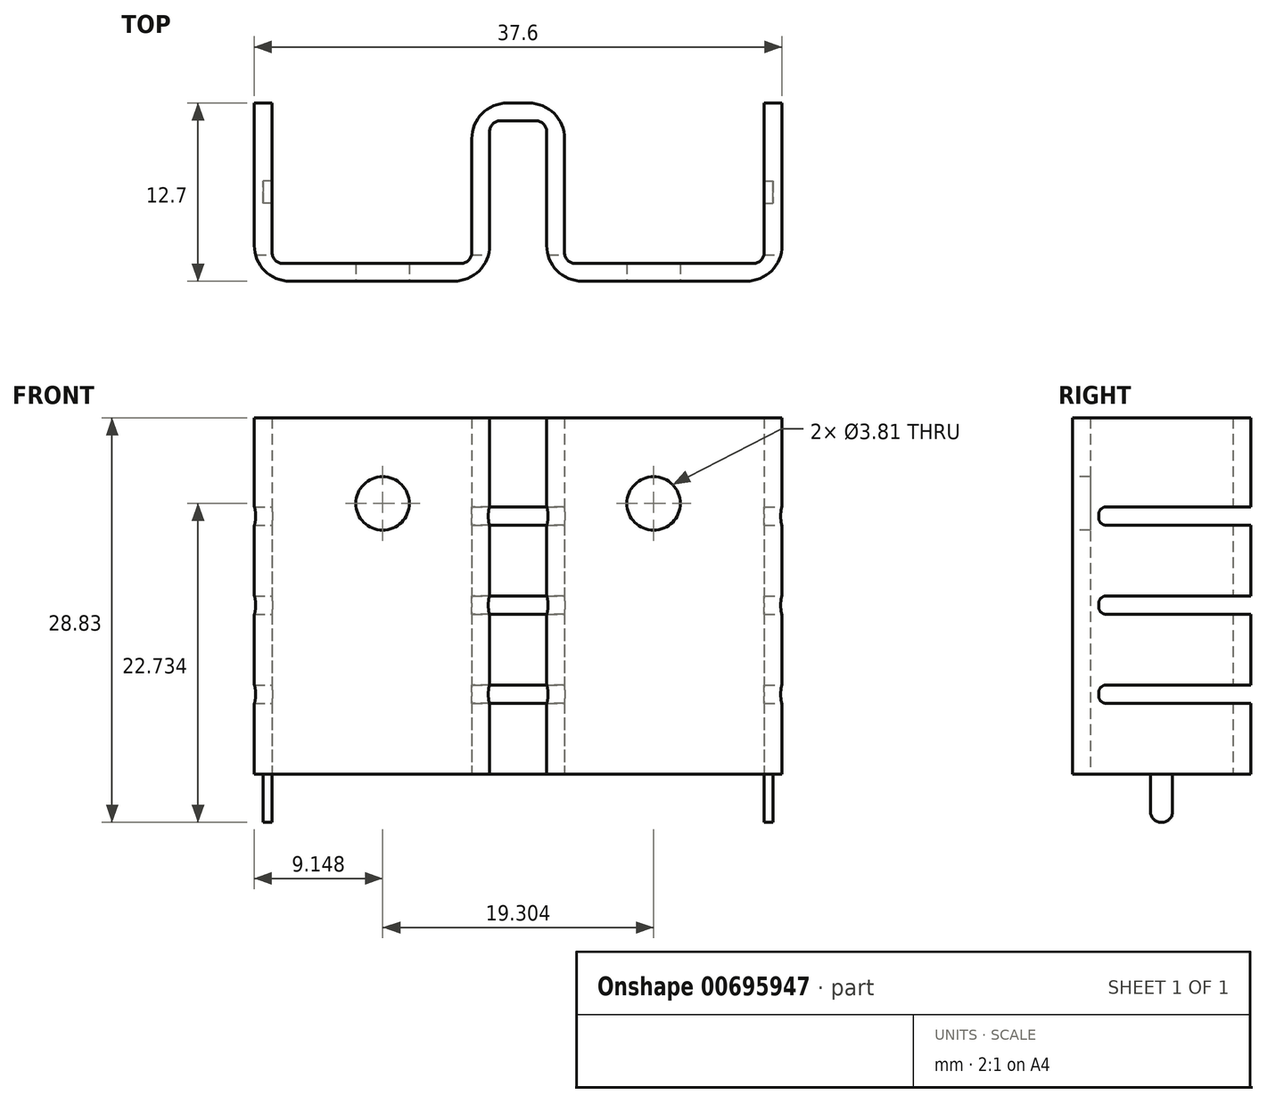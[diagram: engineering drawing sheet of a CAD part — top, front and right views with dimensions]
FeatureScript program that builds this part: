
annotation { "Feature Type Name" : "Feature", "Feature Type Description" : "" }
export const myFeature = defineFeature(function(context is Context, id is Id, definition is map)
    precondition{}
    {
        {
            var Q0;
            Q0=qCreatedBy(makeId("Top.planeOp"),FACE);
            var sketch = newSketch(context, id + "F0", { "sketchPlane" : qUnion([Q0])});
            skLineSegment(sketch, "E0", {"start": v(18.8, 6.35) * mm, "end": v(18.8, -3.81) * mm});
            skLineSegment(sketch, "E1", {"start": v(-18.8, -3.81) * mm, "end": v(-18.8, 6.35) * mm});
            skLineSegment(sketch, "E2", {"start": v(-18.8, 6.35) * mm, "end": v(-17.53, 6.35) * mm});
            skLineSegment(sketch, "E3", {"start": v(-17.53, 6.35) * mm, "end": v(-17.53, -4.32) * mm});
            skLineSegment(sketch, "E4", {"start": v(-16.76, -5.08) * mm, "end": v(-4.06, -5.08) * mm});
            skLineSegment(sketch, "E5", {"start": v(-3.3, -4.32) * mm, "end": v(-3.3, 3.8) * mm});
            skLineSegment(sketch, "E6", {"start": v(-0.76, 6.35) * mm, "end": v(0.76, 6.35) * mm});
            skLineSegment(sketch, "E7", {"start": v(3.3, 3.8) * mm, "end": v(3.3, -4.32) * mm});
            skLineSegment(sketch, "E8", {"start": v(4.06, -5.08) * mm, "end": v(16.76, -5.08) * mm});
            skLineSegment(sketch, "E9", {"start": v(17.53, -4.32) * mm, "end": v(17.53, 6.35) * mm});
            skLineSegment(sketch, "E10", {"start": v(17.53, 6.35) * mm, "end": v(18.8, 6.35) * mm});
            skLineSegment(sketch, "E11", {"start": v(-2.03, -3.81) * mm, "end": v(-2.03, 4.32) * mm});
            skLineSegment(sketch, "E12", {"start": v(-1.27, 5.08) * mm, "end": v(1.27, 5.08) * mm});
            skLineSegment(sketch, "E13", {"start": v(2.03, 4.32) * mm, "end": v(2.03, -3.81) * mm});
            skLineSegment(sketch, "E14", {"start": v(16.26, -6.35) * mm, "end": v(4.57, -6.35) * mm});
            skLineSegment(sketch, "E15", {"start": v(-4.57, -6.35) * mm, "end": v(-16.26, -6.35) * mm});
            skPoint(sketch, "E16.visualSharp", {"position": v(-3.3, 6.35) * mm});
            skArc(sketch, "E16.filletArc", {"start": v(-0.76, 6.35) * mm, "mid": v(-2.56, 5.6) * mm, "end": v(-3.3, 3.8) * mm});
            skPoint(sketch, "E17.visualSharp", {"position": v(3.3, 6.35) * mm});
            skArc(sketch, "E17.filletArc", {"start": v(3.3, 3.8) * mm, "mid": v(2.56, 5.6) * mm, "end": v(0.76, 6.35) * mm});
            skPoint(sketch, "E18.visualSharp", {"position": v(-2.03, 5.08) * mm});
            skArc(sketch, "E18.filletArc", {"start": v(-1.27, 5.08) * mm, "mid": v(-1.8, 4.86) * mm, "end": v(-2.03, 4.32) * mm});
            skPoint(sketch, "E19.visualSharp", {"position": v(2.03, 5.08) * mm});
            skArc(sketch, "E19.filletArc", {"start": v(2.03, 4.32) * mm, "mid": v(1.8, 4.86) * mm, "end": v(1.27, 5.08) * mm});
            skPoint(sketch, "E20.visualSharp", {"position": v(-3.3, -5.08) * mm});
            skArc(sketch, "E20.filletArc", {"start": v(-4.06, -5.08) * mm, "mid": v(-3.53, -4.86) * mm, "end": v(-3.3, -4.32) * mm});
            skPoint(sketch, "E21.visualSharp", {"position": v(-2.03, -6.35) * mm});
            skArc(sketch, "E21.filletArc", {"start": v(-4.57, -6.35) * mm, "mid": v(-2.78, -5.6) * mm, "end": v(-2.03, -3.81) * mm});
            skPoint(sketch, "E22.visualSharp", {"position": v(3.3, -5.08) * mm});
            skArc(sketch, "E22.filletArc", {"start": v(3.3, -4.32) * mm, "mid": v(3.53, -4.86) * mm, "end": v(4.06, -5.08) * mm});
            skPoint(sketch, "E23.visualSharp", {"position": v(2.03, -6.35) * mm});
            skArc(sketch, "E23.filletArc", {"start": v(2.03, -3.81) * mm, "mid": v(2.78, -5.6) * mm, "end": v(4.57, -6.35) * mm});
            skPoint(sketch, "E24.visualSharp", {"position": v(18.8, -6.35) * mm});
            skArc(sketch, "E24.filletArc", {"start": v(16.26, -6.35) * mm, "mid": v(18.05, -5.6) * mm, "end": v(18.8, -3.81) * mm});
            skPoint(sketch, "E25.visualSharp", {"position": v(17.53, -5.08) * mm});
            skArc(sketch, "E25.filletArc", {"start": v(16.76, -5.08) * mm, "mid": v(17.3, -4.86) * mm, "end": v(17.53, -4.32) * mm});
            skPoint(sketch, "E26.visualSharp", {"position": v(-17.53, -5.08) * mm});
            skArc(sketch, "E26.filletArc", {"start": v(-17.53, -4.32) * mm, "mid": v(-17.3, -4.86) * mm, "end": v(-16.76, -5.08) * mm});
            skPoint(sketch, "E27.visualSharp", {"position": v(-18.8, -6.35) * mm});
            skLineSegment(sketch, "E28", {"start": v(-16.26, -6.35) * mm, "end": v(-16.26, -6.35) * mm});
            skLineSegment(sketch, "E29", {"start": v(-18.8, -3.81) * mm, "end": v(-18.8, -3.81) * mm});
            skArc(sketch, "E30.filletArc", {"start": v(-18.8, -3.81) * mm, "mid": v(-18.05, -5.6) * mm, "end": v(-16.26, -6.35) * mm});
            skSolve(sketch);
        }
        {
            var Q0;
            Q0=makeQuery(id+"F0.imprint","IMPRINT",FACE,{"disambiguationData":[TD([[makeQuery(id+"F0.imprint","IMPRINT",EDGE,{"derivedFrom":sQuery(id+"F0.wireOp",EDGE,"E0")}),-1.0]])]});
            extrude(context, id + "F1", {"entities" : qUnion([Q0]), "depth" : 25.4 * mm, "offsetDistance" : 25.4 * mm});
        }
        {
            var Q0;
            Q0=makeQuery(id+"F1.opExtrude","SWEPT_FACE",FACE,{"disambiguationData":[OSD([sQuery(id+"F0.wireOp",EDGE,"E15")])]});
            var sketch = newSketch(context, id + "F2", { "sketchPlane" : qUnion([Q0])});
            skCircle(sketch, "E31", {"center": v(-9.65, 19.3) * mm, "radius": 1.9 * mm});
            skCircle(sketch, "E32", {"center": v(9.65, 19.3) * mm, "radius": 1.9 * mm});
            skSolve(sketch);
        }
        {
            var Q0;
            Q0=makeQuery(id+"F2.imprint","IMPRINT",FACE,{"disambiguationData":[TD([[makeQuery(id+"F2.imprint","IMPRINT",EDGE,{"derivedFrom":sQuery(id+"F2.wireOp",EDGE,"E31")}),1.0]])]});
            var Q1;
            Q1=makeQuery(id+"F2.imprint","IMPRINT",FACE,{"disambiguationData":[TD([[makeQuery(id+"F2.imprint","IMPRINT",EDGE,{"derivedFrom":sQuery(id+"F2.wireOp",EDGE,"E32")}),1.0]])]});
            extrude(context, id + "F3", {"entities" : qUnion([Q0, Q1]), "operationType" : NewBodyOperationType.REMOVE, "oppositeDirection" : true, "depth" : 2.54 * mm, "offsetDistance" : 25.4 * mm});
        }
        {
            var Q0;
            Q0=makeQuery(id+"F1.opExtrude","SWEPT_FACE",FACE,{"disambiguationData":[OSD([sQuery(id+"F0.wireOp",EDGE,"E0")])]});
            var sketch = newSketch(context, id + "F4", { "sketchPlane" : qUnion([Q0])});
            skLineSegment(sketch, "E33.bottom", {"start": v(6.35, 19.05) * mm, "end": v(-3.97, 19.05) * mm});
            skLineSegment(sketch, "E33.top", {"start": v(6.35, 17.76) * mm, "end": v(-3.97, 17.76) * mm});
            skLineSegment(sketch, "E33.left", {"start": v(6.35, 19.05) * mm, "end": v(6.35, 17.76) * mm});
            skLineSegment(sketch, "E33.right", {"start": v(-4.47, 18.54) * mm, "end": v(-4.47, 18.26) * mm});
            skPoint(sketch, "E34.visualSharp", {"position": v(-4.47, 19.05) * mm});
            skArc(sketch, "E34.filletArc", {"start": v(-3.97, 19.05) * mm, "mid": v(-4.33, 18.9) * mm, "end": v(-4.47, 18.54) * mm});
            skPoint(sketch, "E35.visualSharp", {"position": v(-4.47, 17.76) * mm});
            skArc(sketch, "E35.filletArc", {"start": v(-4.47, 18.26) * mm, "mid": v(-4.33, 17.9) * mm, "end": v(-3.97, 17.76) * mm});
            skLineSegment(sketch, "E36.0.1.0", {"start": v(6.35, 12.7) * mm, "end": v(-3.97, 12.7) * mm});
            skLineSegment(sketch, "E36.0.1.1", {"start": v(6.35, 12.7) * mm, "end": v(6.35, 11.4) * mm});
            skLineSegment(sketch, "E36.0.1.2", {"start": v(6.35, 11.4) * mm, "end": v(-3.97, 11.4) * mm});
            skLineSegment(sketch, "E36.0.1.3", {"start": v(-4.47, 12.2) * mm, "end": v(-4.47, 11.91) * mm});
            skArc(sketch, "E36.0.1.4", {"start": v(-4.47, 11.91) * mm, "mid": v(-4.33, 11.56) * mm, "end": v(-3.97, 11.4) * mm});
            skArc(sketch, "E36.0.1.5", {"start": v(-3.97, 12.7) * mm, "mid": v(-4.33, 12.55) * mm, "end": v(-4.47, 12.2) * mm});
            skLineSegment(sketch, "E36.0.2.0", {"start": v(6.35, 6.35) * mm, "end": v(-3.97, 6.35) * mm});
            skLineSegment(sketch, "E36.0.2.1", {"start": v(6.35, 6.35) * mm, "end": v(6.35, 5.06) * mm});
            skLineSegment(sketch, "E36.0.2.2", {"start": v(6.35, 5.06) * mm, "end": v(-3.97, 5.06) * mm});
            skLineSegment(sketch, "E36.0.2.3", {"start": v(-4.47, 5.84) * mm, "end": v(-4.47, 5.56) * mm});
            skArc(sketch, "E36.0.2.4", {"start": v(-4.47, 5.56) * mm, "mid": v(-4.33, 5.2) * mm, "end": v(-3.97, 5.06) * mm});
            skArc(sketch, "E36.0.2.5", {"start": v(-3.97, 6.35) * mm, "mid": v(-4.33, 6.2) * mm, "end": v(-4.47, 5.84) * mm});
            skLineSegment(sketch, "E36.direction1", {"start": v(-3.97, 19.05) * mm, "end": v(21.43, 19.05) * mm, "construction": true});
            skLineSegment(sketch, "E36.direction2", {"start": v(-3.97, 19.05) * mm, "end": v(-3.97, 12.7) * mm, "construction": true});
            skSolve(sketch);
        }
        {
            var Q0;
            {var subQ0=sQuery(id+"F4.wireOp",EDGE,"E33.left");Q0=makeQuery(id+"F4.imprint","IMPRINT",FACE,{"disambiguationData":[TD([[makeQuery(id+"F4.imprint","IMPRINT",EDGE,{"derivedFrom":subQ0}),-1.0]])]});}
            var Q1;
            {var subQ0=sQuery(id+"F4.wireOp",EDGE,"E36.0.1.1");Q1=makeQuery(id+"F4.imprint","IMPRINT",FACE,{"disambiguationData":[TD([[makeQuery(id+"F4.imprint","IMPRINT",EDGE,{"derivedFrom":subQ0}),-1.0]])]});}
            var Q2;
            {var subQ0=sQuery(id+"F4.wireOp",EDGE,"E36.0.2.1");Q2=makeQuery(id+"F4.imprint","IMPRINT",FACE,{"disambiguationData":[TD([[makeQuery(id+"F4.imprint","IMPRINT",EDGE,{"derivedFrom":subQ0}),-1.0]])]});}
            var Q3;
            Q3=makeQuery(id+"F4.imprint","IMPRINT",FACE,{"disambiguationData":[TD([[makeQuery(id+"F4.imprint","IMPRINT",EDGE,{"derivedFrom":sQuery(id+"F4.wireOp",EDGE,"E36.0.2.3")}),1.0]])]});
            var Q4;
            Q4=makeQuery(id+"F4.imprint","IMPRINT",FACE,{"disambiguationData":[TD([[makeQuery(id+"F4.imprint","IMPRINT",EDGE,{"derivedFrom":sQuery(id+"F4.wireOp",EDGE,"E36.0.1.3")}),1.0]])]});
            var Q5;
            Q5=makeQuery(id+"F4.imprint","IMPRINT",FACE,{"disambiguationData":[TD([[makeQuery(id+"F4.imprint","IMPRINT",EDGE,{"derivedFrom":sQuery(id+"F4.wireOp",EDGE,"E33.right")}),1.0]])]});
            extrude(context, id + "F5", {"entities" : qUnion([Q0, Q1, Q2, Q3, Q4, Q5]), "operationType" : NewBodyOperationType.REMOVE, "oppositeDirection" : true, "depth" : 37.6 * mm, "offsetDistance" : 25.4 * mm});
        }
        {
            var Q0;
            Q0=makeQuery(id+"F1.opExtrude","SWEPT_FACE",FACE,{"disambiguationData":[OSD([sQuery(id+"F0.wireOp",EDGE,"E1"),sQuery(id+"F0.wireOp",EDGE,"E29")])]});
            var sketch = newSketch(context, id + "F6", { "sketchPlane" : qUnion([Q0])});
            skLineSegment(sketch, "E37.bottom", {"start": v(0.79, 0) * mm, "end": v(-0.79, 0) * mm});
            skLineSegment(sketch, "E37.top", {"start": v(0.03, -3.43) * mm, "end": v(-0.03, -3.43) * mm});
            skLineSegment(sketch, "E37.left", {"start": v(0.79, 0) * mm, "end": v(0.79, -2.67) * mm});
            skLineSegment(sketch, "E37.right", {"start": v(-0.79, 0) * mm, "end": v(-0.79, -2.67) * mm});
            skPoint(sketch, "E38.visualSharp", {"position": v(0.79, -3.43) * mm});
            skArc(sketch, "E38.filletArc", {"start": v(0.03, -3.43) * mm, "mid": v(0.56, -3.2) * mm, "end": v(0.79, -2.67) * mm});
            skPoint(sketch, "E39.visualSharp", {"position": v(-0.79, -3.43) * mm});
            skArc(sketch, "E39.filletArc", {"start": v(-0.79, -2.67) * mm, "mid": v(-0.56, -3.2) * mm, "end": v(-0.03, -3.43) * mm});
            skLineSegment(sketch, "E40", {"start": v(0.79, 0) * mm, "end": v(3.61, 0) * mm});
            skLineSegment(sketch, "E41", {"start": v(-3.48, 0) * mm, "end": v(-0.79, 0) * mm});
            skSolve(sketch);
        }
        {
            var Q0;
            Q0=makeQuery(id+"F6.imprint","IMPRINT",FACE,{"disambiguationData":[TD([[makeQuery(id+"F6.imprint","IMPRINT",EDGE,{"derivedFrom":sQuery(id+"F6.wireOp",EDGE,"E37.bottom")}),1.0]])]});
            extrude(context, id + "F7", {"entities" : qUnion([Q0]), "operationType" : NewBodyOperationType.ADD, "oppositeDirection" : true, "depth" : 1.27 * mm, "offsetDistance" : 25.4 * mm});
        }
        {
            var Q0;
            Q0=makeQuery(id+"F6.imprint","IMPRINT",FACE,{"disambiguationData":[TD([[makeQuery(id+"F6.imprint","IMPRINT",EDGE,{"derivedFrom":sQuery(id+"F6.wireOp",EDGE,"E37.bottom")}),1.0]])]});
            extrude(context, id + "F8", {"entities" : qUnion([Q0]), "operationType" : NewBodyOperationType.REMOVE, "oppositeDirection" : true, "depth" : 0.64 * mm, "offsetDistance" : 25.4 * mm});
        }
        {
            var Q0;
            {var subQ2=sQuery(id+"F0.wireOp",EDGE,"E0");Q0=makeQuery(id+"F5.boolean.opBoolean","SPLIT",FACE,{"disambiguationData":[TD([makeQuery(id+"F5.opExtrude","SWEPT_FACE",FACE,{"disambiguationData":[OSD([sQuery(id+"F4.wireOp",EDGE,"E36.0.2.2")])]})])],"derivedFrom":makeQuery(id+"F1.opExtrude","SWEPT_FACE",FACE,{"disambiguationData":[OSD([subQ2])]})});}
            var sketch = newSketch(context, id + "F9", { "sketchPlane" : qUnion([Q0])});
            skLineSegment(sketch, "E42.bottom", {"start": v(0.79, 0) * mm, "end": v(-0.79, 0) * mm});
            skLineSegment(sketch, "E42.top", {"start": v(0.03, -3.43) * mm, "end": v(-0.03, -3.43) * mm});
            skLineSegment(sketch, "E42.left", {"start": v(0.79, 0) * mm, "end": v(0.79, -2.67) * mm});
            skLineSegment(sketch, "E42.right", {"start": v(-0.79, 0) * mm, "end": v(-0.79, -2.67) * mm});
            skPoint(sketch, "E43.visualSharp", {"position": v(-0.79, -3.43) * mm});
            skArc(sketch, "E43.filletArc", {"start": v(-0.79, -2.67) * mm, "mid": v(-0.56, -3.2) * mm, "end": v(-0.03, -3.43) * mm});
            skPoint(sketch, "E44.visualSharp", {"position": v(0.79, -3.43) * mm});
            skArc(sketch, "E44.filletArc", {"start": v(0.03, -3.43) * mm, "mid": v(0.56, -3.2) * mm, "end": v(0.79, -2.67) * mm});
            skSolve(sketch);
        }
        {
            var Q0;
            Q0=makeQuery(id+"F9.imprint","IMPRINT",FACE,{"disambiguationData":[TD([[makeQuery(id+"F9.imprint","IMPRINT",EDGE,{"derivedFrom":sQuery(id+"F9.wireOp",EDGE,"E42.bottom")}),1.0]])]});
            extrude(context, id + "F10", {"entities" : qUnion([Q0]), "oppositeDirection" : true, "depth" : 1.27 * mm, "offsetDistance" : 25.4 * mm});
        }
        {
            var Q0;
            Q0=makeQuery(id+"F10.opExtrude","CAP_FACE",FACE,{"disambiguationData":[OSD([sQuery(id+"F9.wireOp",EDGE,"E42.bottom"),sQuery(id+"F9.wireOp",EDGE,"E42.top"),sQuery(id+"F9.wireOp",EDGE,"E42.left"),sQuery(id+"F9.wireOp",EDGE,"E42.right"),sQuery(id+"F9.wireOp",EDGE,"E43.filletArc"),sQuery(id+"F9.wireOp",EDGE,"E44.filletArc")])],"isStart":true});
            extrude(context, id + "F11", {"entities" : qUnion([Q0]), "operationType" : NewBodyOperationType.REMOVE, "oppositeDirection" : true, "depth" : 0.64 * mm, "offsetDistance" : 25.4 * mm});
        }
    });
